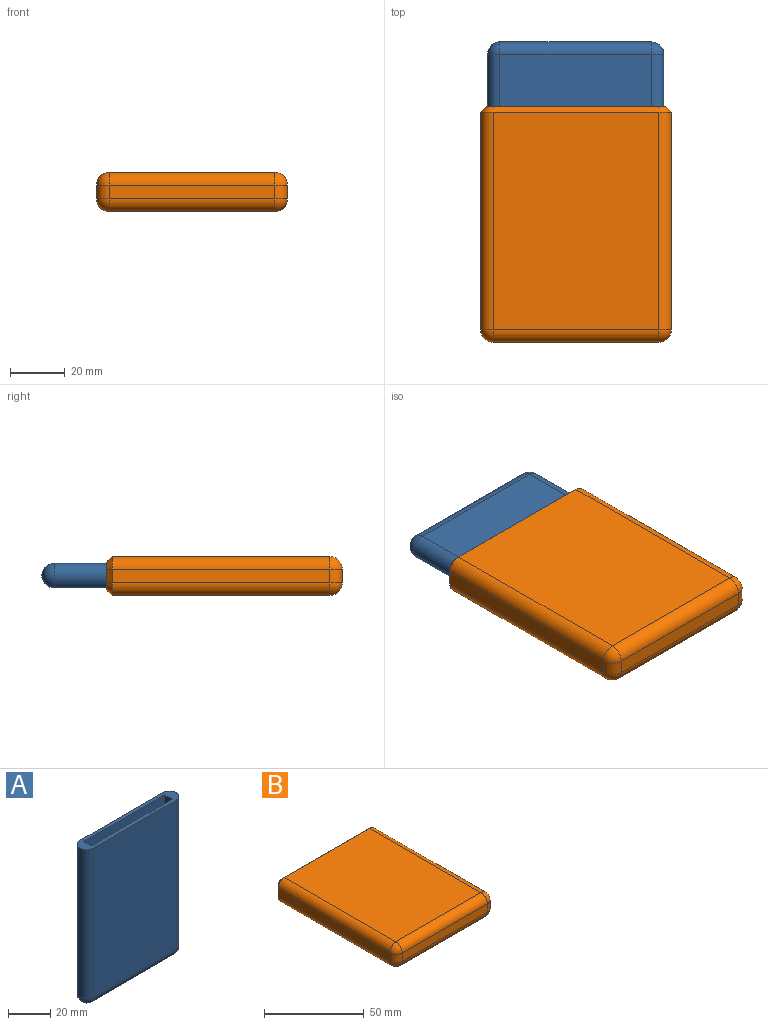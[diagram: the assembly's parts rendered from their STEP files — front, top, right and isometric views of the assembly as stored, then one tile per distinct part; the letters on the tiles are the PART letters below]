
ASSEMBLY  parts=2 mates=1
PART A: 13 faces, bbox 64.2x8.9x90.7 mm
  f0: plane 54x5.08mm, normal (0,0,1), area 274.3mm2, adj f2,f3,f11,f12
  f1: plane 64.16x8.89mm, normal (0,0,1), area 279.1mm2, adj f2,f3,f4,f5,f6,f7,f11,f12
  f2: plane 85.62x5.08mm, normal (-1,0,0), area 435mm2, adj f0,f1,f11,f12
  f3: plane 85.62x5.08mm, normal (1,0,0), area 435mm2, adj f0,f1,f11,f12
  f4: plane 86.26x55.27mm, normal (0,-1,0), area 4767.5mm2, adj f1,f6,f7,f10
  f5: plane 86.26x55.27mm, normal (0,1,0), area 4767.5mm2, adj f1,f6,f7,f10
  f6: cylinder r=4.45mm len=86.26mm, axis (0,0,1), area 1204.5mm2, adj f1,f4,f5,f8
  f7: cylinder r=4.45mm len=86.26mm, axis (0,0,-1), area 1204.5mm2, adj f1,f4,f5,f9
  f8: sphere r=4.45mm, area 62.1mm2, adj f6,f10
  f9: sphere r=4.45mm, area 62.1mm2, adj f7,f10
  f10: cylinder r=4.45mm len=55.27mm, axis (-1,0,0), area 771.8mm2, adj f4,f5,f8,f9
  f11: plane 85.62x54mm, normal (0,-1,0), area 4623.7mm2, adj f0,f1,f2,f3
  f12: plane 85.62x54mm, normal (0,1,0), area 4623.7mm2, adj f0,f1,f2,f3
PART B: 35 faces, bbox 69.5x85.6x14.2 mm
  f0: plane 79.5x55.52mm, normal (0,0,-1), area 4414.4mm2, adj f3,f6,f7,f34
  f1: plane 79.5x55.52mm, normal (0,0,1), area 4414.4mm2, adj f4,f5,f7,f34
  f2: plane 79.5x0.25mm, normal (1,0,0), area 20.2mm2, adj f5,f6,f7,f34
  f3: cylinder r=4.45mm len=79.5mm, axis (0,1,0), area 555.1mm2, adj f0,f7,f8,f34
  f4: cylinder r=4.45mm len=79.5mm, axis (0,-1,0), area 555.1mm2, adj f1,f7,f8,f34
  f5: cylinder r=4.45mm len=79.5mm, axis (0,1,0), area 555.1mm2, adj f1,f2,f7,f34
  f6: cylinder r=4.45mm len=79.5mm, axis (0,-1,0), area 555.1mm2, adj f0,f2,f7,f34
  f7: plane 65.43x10.16mm, normal (0,1,0), area 87.2mm2, adj f0,f1,f2,f3,f4,f5,f6,f8
  f8: plane 79.5x0.25mm, normal (-1,0,0), area 20.2mm2, adj f3,f4,f7,f34
  f9: plane 79.02x5.08mm, normal (1,0,0), area 401.4mm2, adj f14,f18,f19,f27
  f10: plane 79.02x60.35mm, normal (0,0,1), area 4768.9mm2, adj f14,f16,f17,f28
  f11: plane 79.02x5.08mm, normal (-1,0,0), area 401.4mm2, adj f16,f22,f25,f32
  f12: plane 79.02x60.35mm, normal (0,0,-1), area 4768.9mm2, adj f19,f23,f25,f31
  f13: plane 60.35x5.08mm, normal (0,-1,0), area 306.6mm2, adj f17,f18,f22,f23
  f14: cylinder r=4.57mm len=79.02mm, axis (0,-1,0), area 567.5mm2, adj f9,f10,f15,f26
  f15: sphere r=4.57mm, area 32.8mm2, adj f14,f17,f18
  f16: cylinder r=4.57mm len=79.02mm, axis (0,1,0), area 567.5mm2, adj f10,f11,f20,f30
  f17: cylinder r=4.57mm len=60.35mm, axis (1,0,0), area 433.4mm2, adj f10,f13,f15,f20
  f18: cylinder r=4.57mm len=5.08mm, axis (0,0,-1), area 36.5mm2, adj f9,f13,f15,f21
  f19: cylinder r=4.57mm len=79.02mm, axis (0,1,0), area 567.5mm2, adj f9,f12,f21,f29
  f20: sphere r=4.57mm, area 32.8mm2, adj f16,f17,f22
  f21: sphere r=4.57mm, area 32.8mm2, adj f18,f19,f23
  f22: cylinder r=4.57mm len=5.08mm, axis (0,0,1), area 36.5mm2, adj f11,f13,f20,f24
  f23: cylinder r=4.57mm len=60.35mm, axis (-1,0,0), area 433.4mm2, adj f12,f13,f21,f24
  f24: sphere r=4.57mm, area 32.8mm2, adj f22,f23,f25
  f25: cylinder r=4.57mm len=79.02mm, axis (0,-1,0), area 567.5mm2, adj f11,f12,f24,f33
  f26: cone r=2.54mm half-angle=45deg, axis (0,-1,0), area 16.1mm2, adj f7,f14,f27,f28
  f27: plane 5.08x2.03mm, normal (0.71,0.71,0), area 14.6mm2, adj f7,f9,f26,f29
  f28: plane 60.35x2.03mm, normal (0,0.71,0.71), area 173.4mm2, adj f7,f10,f26,f30
  f29: cone r=2.54mm half-angle=45deg, axis (0,-1,0), area 16.1mm2, adj f7,f19,f27,f31
  f30: cone r=2.54mm half-angle=45deg, axis (0,-1,0), area 16.1mm2, adj f7,f16,f28,f32
  f31: plane 60.35x2.03mm, normal (0,0.71,-0.71), area 173.4mm2, adj f7,f12,f29,f33
  f32: plane 5.08x2.03mm, normal (-0.71,0.71,0), area 14.6mm2, adj f7,f11,f30,f33
  f33: cone r=2.54mm half-angle=45deg, axis (0,-1,0), area 16.1mm2, adj f7,f25,f31,f32
  f34: plane 64.41x9.14mm, normal (0,1,0), area 572mm2, adj f0,f1,f2,f3,f4,f5,f6,f8
PLACE A rot(axis=(1,0,0),90deg) t=(-27.55,18.57,12.46)mm
PLACE B t=(-32.63,0,4.59)mm fixed
MATE slider A.f1 <-> B.f7  axis (0,-1,0) through (-28.18,-67.06,13.73)mm
